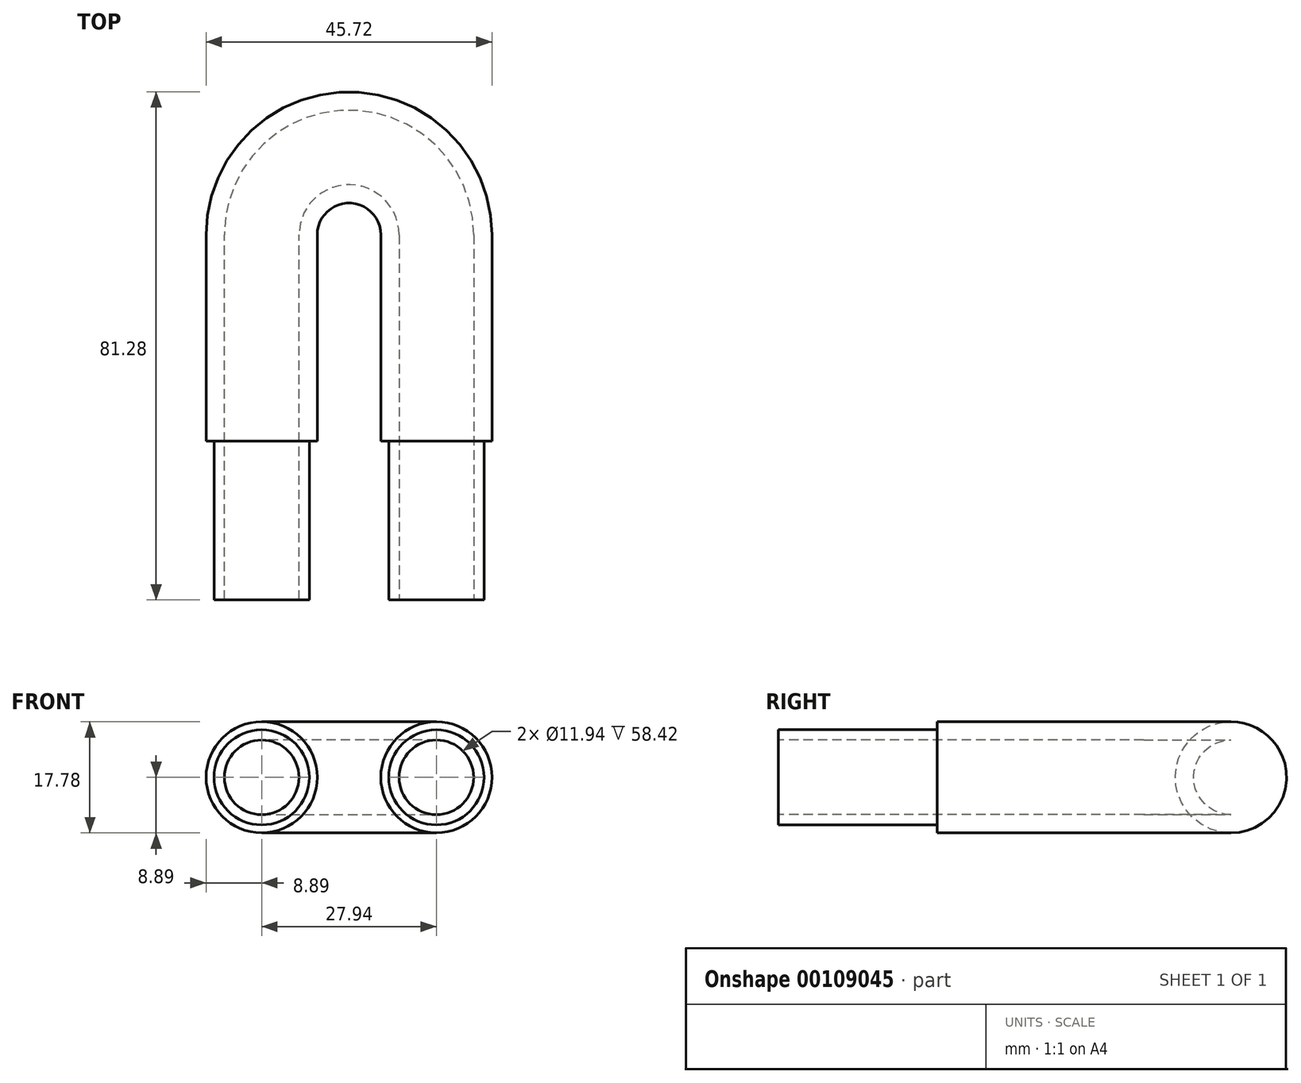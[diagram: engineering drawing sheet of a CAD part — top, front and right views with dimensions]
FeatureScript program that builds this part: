
annotation { "Feature Type Name" : "Feature", "Feature Type Description" : "" }
export const myFeature = defineFeature(function(context is Context, id is Id, definition is map)
    precondition{}
    {
        {
            var Q0;
            Q0=qCreatedBy(makeId("Front.planeOp"),FACE);
            var sketch = newSketch(context, id + "F0", { "sketchPlane" : qUnion([Q0])});
            skCircle(sketch, "E0", {"center": v(0, 0) * mm, "radius": 5.97 * mm});
            skCircle(sketch, "E1", {"center": v(0, 0) * mm, "radius": 8.9 * mm});
            skSolve(sketch);
        }
        {
            var Q0;
            Q0=qCreatedBy(makeId("Top.planeOp"),FACE);
            var sketch = newSketch(context, id + "F1", { "sketchPlane" : qUnion([Q0])});
            skLineSegment(sketch, "E2", {"start": v(0, 0) * mm, "end": v(0, 33.02) * mm});
            skArc(sketch, "E3", {"start": v(0, 33.02) * mm, "mid": v(13.97, 47) * mm, "end": v(27.94, 33.02) * mm});
            skLineSegment(sketch, "E4", {"start": v(27.94, 33.02) * mm, "end": v(27.94, 0) * mm});
            skSolve(sketch);
        }
        {
            var Q0;
            Q0=makeQuery(id+"F0.imprint","IMPRINT",FACE,{"disambiguationData":[TD([[makeQuery(id+"F0.imprint","IMPRINT",EDGE,{"derivedFrom":sQuery(id+"F0.wireOp",EDGE,"E0")}),-1.0]])]});
            var Q1;
            Q1=sQuery(id+"F1.wireOp",EDGE,"E2");
            var Q2;
            Q2=sQuery(id+"F1.wireOp",EDGE,"E3");
            var Q3;
            Q3=sQuery(id+"F1.wireOp",EDGE,"E4");
            sweep(context, id + "F2", {"profiles" : qUnion([Q0]), "path" : qUnion([Q1, Q2, Q3])});
        }
        {
            var Q0;
            Q0=makeQuery(id+"F2.opSweep","CAP_FACE",FACE,{"disambiguationData":[OSD([sQuery(id+"F0.wireOp",EDGE,"E0"),sQuery(id+"F0.wireOp",EDGE,"E1"),sQuery(id+"F1.wireOp",VERTEX,"E2.start")])],"isStart":true});
            var sketch = newSketch(context, id + "F3", { "sketchPlane" : qUnion([Q0])});
            skCircle(sketch, "E5", {"center": v(0, 0) * mm, "radius": 7.62 * mm});
            skSolve(sketch);
        }
        {
            var Q0;
            Q0=makeQuery(id+"F2.opSweep","CAP_FACE",FACE,{"disambiguationData":[OSD([sQuery(id+"F0.wireOp",EDGE,"E0"),sQuery(id+"F0.wireOp",EDGE,"E1"),sQuery(id+"F1.wireOp",VERTEX,"E4.end")])],"isStart":false});
            var sketch = newSketch(context, id + "F4", { "sketchPlane" : qUnion([Q0])});
            skCircle(sketch, "E6", {"center": v(27.94, 0) * mm, "radius": 7.62 * mm});
            skSolve(sketch);
        }
        {
            var Q0;
            Q0=makeQuery(id+"F3.imprint","IMPRINT",FACE,{"disambiguationData":[TD([[makeQuery(id+"F3.imprint","IMPRINT",EDGE,{"derivedFrom":sQuery(id+"F3.wireOp",EDGE,"E5")}),1.0]])]});
            var Q1;
            Q1=makeQuery(id+"F4.imprint","IMPRINT",FACE,{"disambiguationData":[TD([[makeQuery(id+"F4.imprint","IMPRINT",EDGE,{"derivedFrom":sQuery(id+"F4.wireOp",EDGE,"E6")}),1.0]])]});
            extrude(context, id + "F5", {"entities" : qUnion([Q0, Q1]), "operationType" : NewBodyOperationType.ADD, "depth" : 25.4 * mm});
        }
    });
